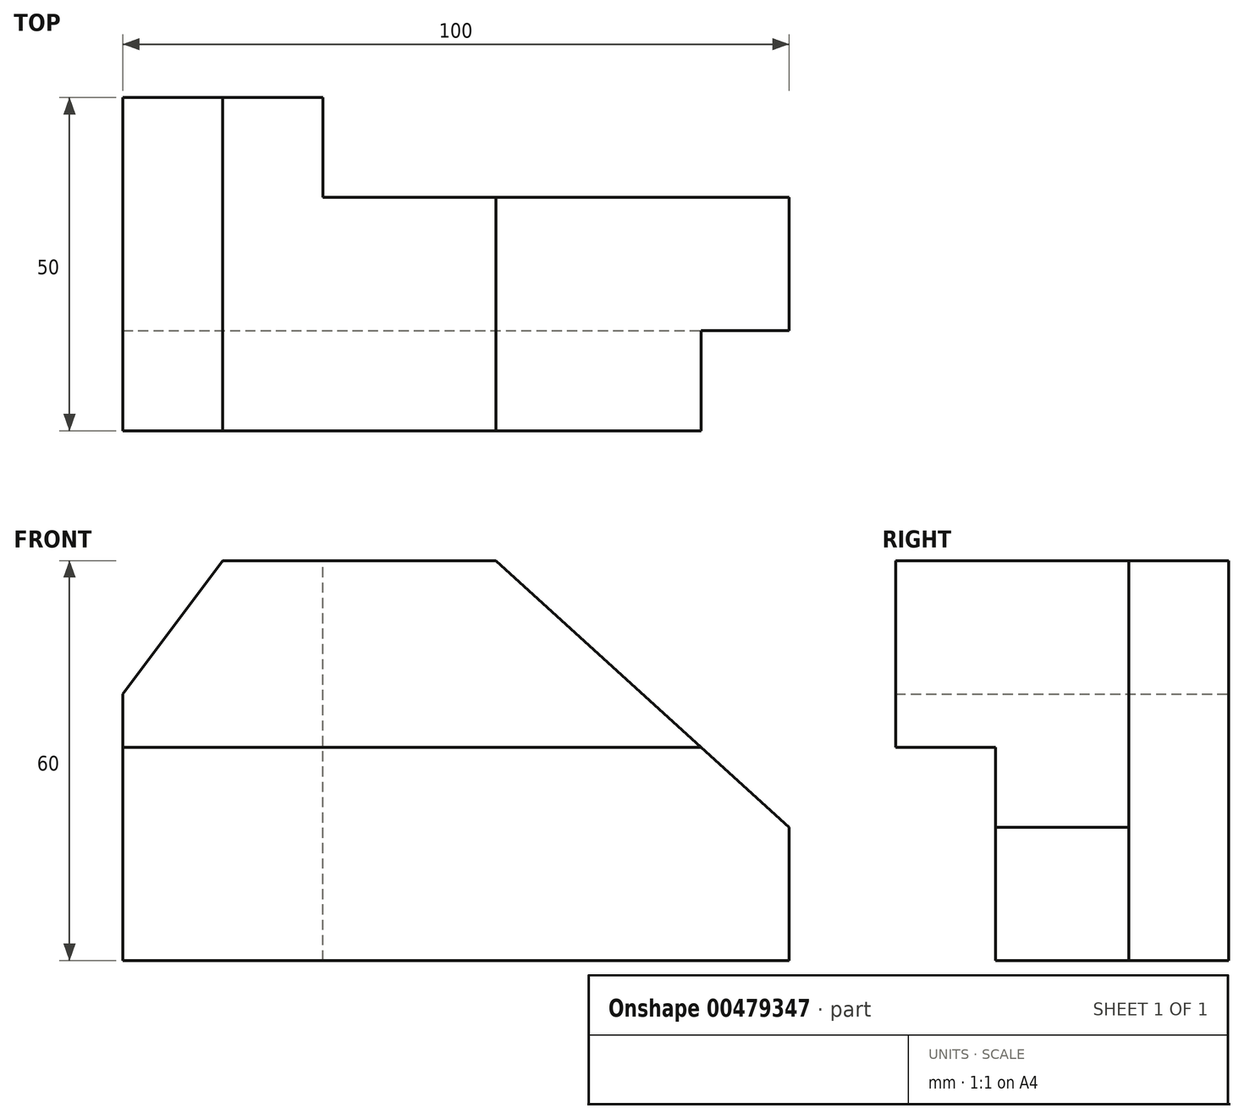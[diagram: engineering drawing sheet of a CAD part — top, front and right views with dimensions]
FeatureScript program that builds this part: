
annotation { "Feature Type Name" : "Feature", "Feature Type Description" : "" }
export const myFeature = defineFeature(function(context is Context, id is Id, definition is map)
    precondition{}
    {
        {
            var Q0;
            Q0=qCreatedBy(makeId("Front.planeOp"),FACE);
            var sketch = newSketch(context, id + "F0", { "sketchPlane" : qUnion([Q0])});
            skLineSegment(sketch, "E0.bottom", {"start": v(0, 0) * mm, "end": v(100, 0) * mm});
            skLineSegment(sketch, "E0.top", {"start": v(0, 60) * mm, "end": v(100, 60) * mm});
            skLineSegment(sketch, "E0.left", {"start": v(0, 0) * mm, "end": v(0, 60) * mm});
            skLineSegment(sketch, "E0.right", {"start": v(100, 0) * mm, "end": v(100, 60) * mm});
            skSolve(sketch);
        }
        {
            var Q0;
            Q0 = qSketchRegion(id + "F0", true);
            extrude(context, id + "F1", {"entities" : qUnion([Q0]), "depth" : 50 * mm});
        }
        {
            var Q0;
            Q0=makeQuery(id+"F1.opExtrude","SWEPT_FACE",FACE,{"disambiguationData":[OSD([sQuery(id+"F0.wireOp",EDGE,"E0.right")])]});
            var sketch = newSketch(context, id + "F2", { "sketchPlane" : qUnion([Q0])});
            skLineSegment(sketch, "E1.bottom", {"start": v(-50, 0) * mm, "end": v(-35, 0) * mm});
            skLineSegment(sketch, "E1.top", {"start": v(-50, 32) * mm, "end": v(-35, 32) * mm});
            skLineSegment(sketch, "E1.left", {"start": v(-50, 0) * mm, "end": v(-50, 32) * mm});
            skLineSegment(sketch, "E1.right", {"start": v(-35, 0) * mm, "end": v(-35, 32) * mm});
            skSolve(sketch);
        }
        {
            var Q0;
            Q0 = qSketchRegion(id + "F2", true);
            extrude(context, id + "F3", {"entities" : qUnion([Q0]), "operationType" : NewBodyOperationType.REMOVE, "endBound" : BoundingType.THROUGH_ALL, "oppositeDirection" : true, "depth" : 25 * mm});
        }
        {
            var Q0;
            Q0=makeQuery(id+"F1.opExtrude","SWEPT_FACE",FACE,{"disambiguationData":[OSD([sQuery(id+"F0.wireOp",EDGE,"E0.top")])]});
            var sketch = newSketch(context, id + "F4", { "sketchPlane" : qUnion([Q0])});
            skLineSegment(sketch, "E2.bottom", {"start": v(100, 0) * mm, "end": v(30, 0) * mm});
            skLineSegment(sketch, "E2.top", {"start": v(100, -15) * mm, "end": v(30, -15) * mm});
            skLineSegment(sketch, "E2.left", {"start": v(100, 0) * mm, "end": v(100, -15) * mm});
            skLineSegment(sketch, "E2.right", {"start": v(30, 0) * mm, "end": v(30, -15) * mm});
            skSolve(sketch);
        }
        {
            var Q0;
            Q0 = qSketchRegion(id + "F4", true);
            extrude(context, id + "F5", {"entities" : qUnion([Q0]), "operationType" : NewBodyOperationType.REMOVE, "endBound" : BoundingType.THROUGH_ALL, "oppositeDirection" : true, "depth" : 25 * mm});
        }
        {
            var Q0;
            Q0=makeQuery(id+"F1.opExtrude","SWEPT_EDGE",EDGE,{"disambiguationData":[OSD([sQuery(id+"F0.wireOp",EDGE,"E0.top"),sQuery(id+"F0.wireOp",EDGE,"E0.left")])]});
            chamfer(context, id + "F6", {"entities" : qUnion([Q0]), "chamferType" : ChamferType.TWO_OFFSETS, "width1" : 20 * mm, "oppositeDirection" : false, "width2" : 15 * mm, "tangentPropagation" : true});
        }
        {
            var Q0;
            Q0=makeQuery(id+"F1.opExtrude","SWEPT_EDGE",EDGE,{"disambiguationData":[OSD([sQuery(id+"F0.wireOp",EDGE,"E0.top"),sQuery(id+"F0.wireOp",EDGE,"E0.right")])]});
            chamfer(context, id + "F7", {"entities" : qUnion([Q0]), "chamferType" : ChamferType.TWO_OFFSETS, "width1" : 44 * mm, "oppositeDirection" : false, "width2" : 40 * mm, "tangentPropagation" : true});
        }
    });
